# Revit family: Construction_Other_Sjobergs_Circular_Saw
name_source: partatom
category: Specialty Equipment
revit_build: Autodesk Revit 2017 (Build: 20190508_0315(x64)
units: mm (PartAtom-declared; Revit-internal decimal feet)

## family parameters
Always vertical = Yes
Cut with Voids When Loaded = No
OmniClass Number = 23.45.30.14.11
OmniClass Title = Commercial Dishwashers
Part Type = Normal
Room Calculation Point = No
Round Connector Dimension = Use Diameter
Shared = No
Work Plane-Based = No

## types (1)
- 37040 EJCA Circular Saw L 18
    AssetType = Movable
    BIMObjectName = Construction_Other_Sjobergs_Circular_Saw
    Brand = EJCA
    Category = Machines
    CircularSawBlade = Ø 300 mm
    CircularSawSizes = Saw table is 580x740 mm. Working height 870 mm.
    Color = Green
    ConnectionSocketSuction = Ø 100 mm
    Constituents = Protective Cover CHO 40 - Equipped with sight glass, built-in work lighting, connection socket for chip extraction and a roller in the front edge of the hood. Adjustament table (length 850-1250mm).
    ConvergoRefNr = 0184-2005-0024-SE
    Cost = 0 $
    DurationUnit = Year
    ElectricalDeviceNominalPower = 2200 W
    Features = The circular saw blade can be raised and lowered with a crank.The stable cleavage content is equipped with a magnifying magnifier to facilitate accurate reading.The machine is delivered with a carbide blade.CE-standard.
    Finish = Cast iron
    HasProtectiveEarth = Yes
    IP_Code = IP 66
    IfcExportAs = IfcFurnishingElementType
    IfcExportType = TABLE
    MachineryMainMaterial = Green metal
    MachineryQuaternaryMaterial = Clearance
    MachinerySecondaryMaterial = Black Metal
    MachineryTertiaryMaterial = Stainless Steel
    Manufacturer = Sjöbergs
    ManufacturerName = Sjöbergs
    ManufacturerURL = https://www.sjobergs.se
    Material = Metal, plastic
    Model = 37040 EJCA Circular Saw L 18
    ModelReference = 37040
    NBSDescription = School art, design and technology tables and workbenches;
    NBSReference = 45-35-20/320
    Name = Sjobergs_Circular_Saw
    NominalCurrent = 0 A
    NominalDepth = 770 mm
    NominalFrequencyRange = 0 Hz
    NominalHeight = 1160 mm
    NominalVoltage = 230 V
    NominalWidth = 815 mm
    NumberOfPoles = 0
    PhaseAngle = 0.00°
    ProductDatasheet = https://www.sjobergs.se
    ProductInformation = A Swedish-made, strong and stable circular saw with table made of vibration-inhibiting cast iron, well machined by planing, an old machining method that gives the absolute best result.
    SawSpindle = 30 mm
    Shape = Sculptured
    Size = 815x770x1160 mm
    URL = https://www.sjobergs.se
    Uniclass2 = Pr_40_50_21
    Uniclass2015Description = Desks, Tables And Worktops
    Uniclass2015Reference = Pr_40_50_21_76
    UsageCurrent = 0 A
    Version = 1
    VersionDate = 01/07/2020
    WarrantyDurationUnit = Year
    Weight = 155.0 kg

## geometry (parser evidence)
native form markers: Sweep x3
no freeform markers — native parametric forms only
